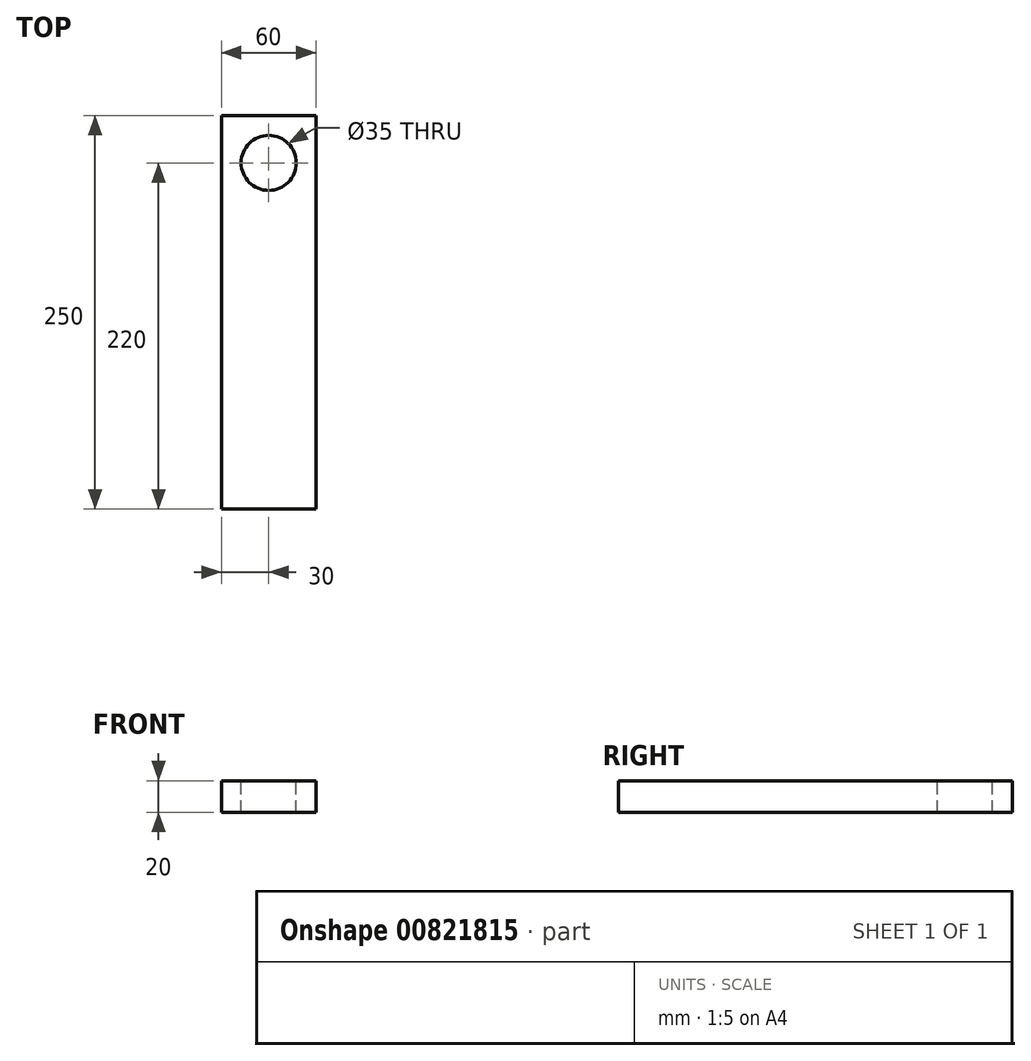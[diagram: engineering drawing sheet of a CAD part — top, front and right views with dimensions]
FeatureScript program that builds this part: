
annotation { "Feature Type Name" : "Feature", "Feature Type Description" : "" }
export const myFeature = defineFeature(function(context is Context, id is Id, definition is map)
    precondition{}
    {
        {
            var Q0;
            Q0=qCreatedBy(makeId("Top.planeOp"),FACE);
            var sketch = newSketch(context, id + "F0", { "sketchPlane" : qUnion([Q0])});
            skLineSegment(sketch, "E0.bottom", {"start": v(30, -125) * mm, "end": v(-30, -125) * mm});
            skLineSegment(sketch, "E0.top", {"start": v(30, 125) * mm, "end": v(-30, 125) * mm});
            skLineSegment(sketch, "E0.left", {"start": v(30, -125) * mm, "end": v(30, 125) * mm});
            skLineSegment(sketch, "E0.right", {"start": v(-30, -125) * mm, "end": v(-30, 125) * mm});
            skPoint(sketch, "E0.middle", {"position": v(0, 0) * mm});
            skSolve(sketch);
        }
        {
            var Q0;
            Q0=makeQuery(id+"F0.imprint","IMPRINT",FACE,{"disambiguationData":[TD([[makeQuery(id+"F0.imprint","IMPRINT",EDGE,{"derivedFrom":sQuery(id+"F0.wireOp",EDGE,"E0.bottom")}),-1.0]])]});
            extrude(context, id + "F1", {"entities" : qUnion([Q0]), "depth" : 20 * mm, "offsetDistance" : 25 * mm});
        }
        {
            var Q0;
            Q0=makeQuery(id+"F1.opExtrude","CAP_FACE",FACE,{"disambiguationData":[OSD([sQuery(id+"F0.wireOp",EDGE,"E0.bottom"),sQuery(id+"F0.wireOp",EDGE,"E0.top"),sQuery(id+"F0.wireOp",EDGE,"E0.left"),sQuery(id+"F0.wireOp",EDGE,"E0.right")])],"isStart":false});
            var sketch = newSketch(context, id + "F2", { "sketchPlane" : qUnion([Q0])});
            skLineSegment(sketch, "E1", {"start": v(-30, 125) * mm, "end": v(0, 95) * mm, "construction": true});
            skCircle(sketch, "E2", {"center": v(0, 95) * mm, "radius": 17.5 * mm});
            skSolve(sketch);
        }
        {
            var Q0;
            Q0=makeQuery(id+"F2.imprint","IMPRINT",FACE,{"disambiguationData":[TD([[makeQuery(id+"F2.imprint","IMPRINT",EDGE,{"derivedFrom":sQuery(id+"F2.wireOp",EDGE,"E2")}),1.0]])]});
            extrude(context, id + "F3", {"entities" : qUnion([Q0]), "operationType" : NewBodyOperationType.REMOVE, "endBound" : BoundingType.UP_TO_NEXT, "oppositeDirection" : true, "depth" : 25 * mm, "offsetDistance" : 25 * mm});
        }
    });
